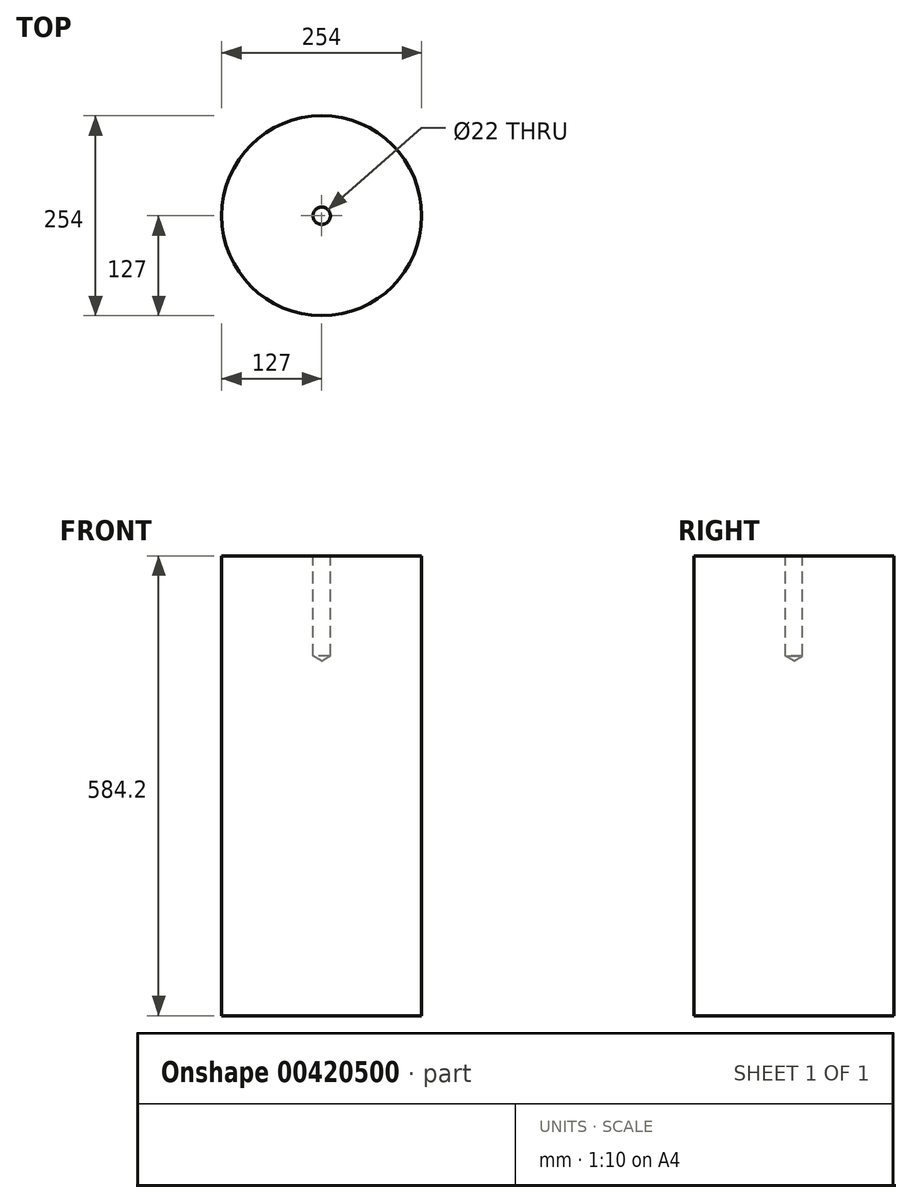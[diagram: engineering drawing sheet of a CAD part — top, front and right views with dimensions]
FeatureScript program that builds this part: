
annotation { "Feature Type Name" : "Feature", "Feature Type Description" : "" }
export const myFeature = defineFeature(function(context is Context, id is Id, definition is map)
    precondition{}
    {
        {
            var Q0;
            Q0=qCreatedBy(makeId("Top.planeOp"),FACE);
            var sketch = newSketch(context, id + "F0", { "sketchPlane" : qUnion([Q0])});
            skCircle(sketch, "E0", {"center": v(0, 0) * mm, "radius": 127 * mm});
            skSolve(sketch);
        }
        {
            var Q0;
            Q0=makeQuery(id+"F0.imprint","IMPRINT",FACE,{"disambiguationData":[TD([[makeQuery(id+"F0.imprint","IMPRINT",EDGE,{"derivedFrom":sQuery(id+"F0.wireOp",EDGE,"E0")}),1.0]])]});
            extrude(context, id + "F1", {"entities" : qUnion([Q0]), "endBound" : BoundingType.SYMMETRIC, "depth" : 584.2 * mm});
        }
        {
            var Q0;
            Q0=makeQuery(id+"F1.opExtrude","CAP_FACE",FACE,{"disambiguationData":[OSD([sQuery(id+"F0.wireOp",EDGE,"E0")])],"isStart":false});
            var sketch = newSketch(context, id + "F2", { "sketchPlane" : qUnion([Q0])});
            skPoint(sketch, "E1", {"position": v(0, 0) * mm});
            skSolve(sketch);
        }
        {
            var Q0;
            Q0=sQuery(id+"F2.wireOp",VERTEX,"E1");
            var Q1;
            Q1=makeQuery(id+"F1.opExtrude","SWEPT_BODY",BODY,{"disambiguationData":[OSD([sQuery(id+"F0.wireOp",EDGE,"E0")])]});
            hole(context, id + "F3", {"style" : HoleStyle.SIMPLE, "endStyle" : HoleEndStyle.BLIND, "standardTappedOrClearance" : lookupTablePath({ "standard" : "ISO", "fit" : "Normal", "size" : "M20", "type" : "Clearance" }), "standardBlindInLast" : lookupTablePath({ "fit" : "Standard", "standard" : "ISO", "size" : "M20", "type" : "Clearance" }), "holeDiameter" : 22 * mm, "holeDepth" : 127 * mm, "isTappedThrough" : true, "tappedDepth" : 12.7 * mm, "tapClearance" : 3, "locations" : qUnion([Q0]), "scope" : qUnion([Q1])});
        }
    });
